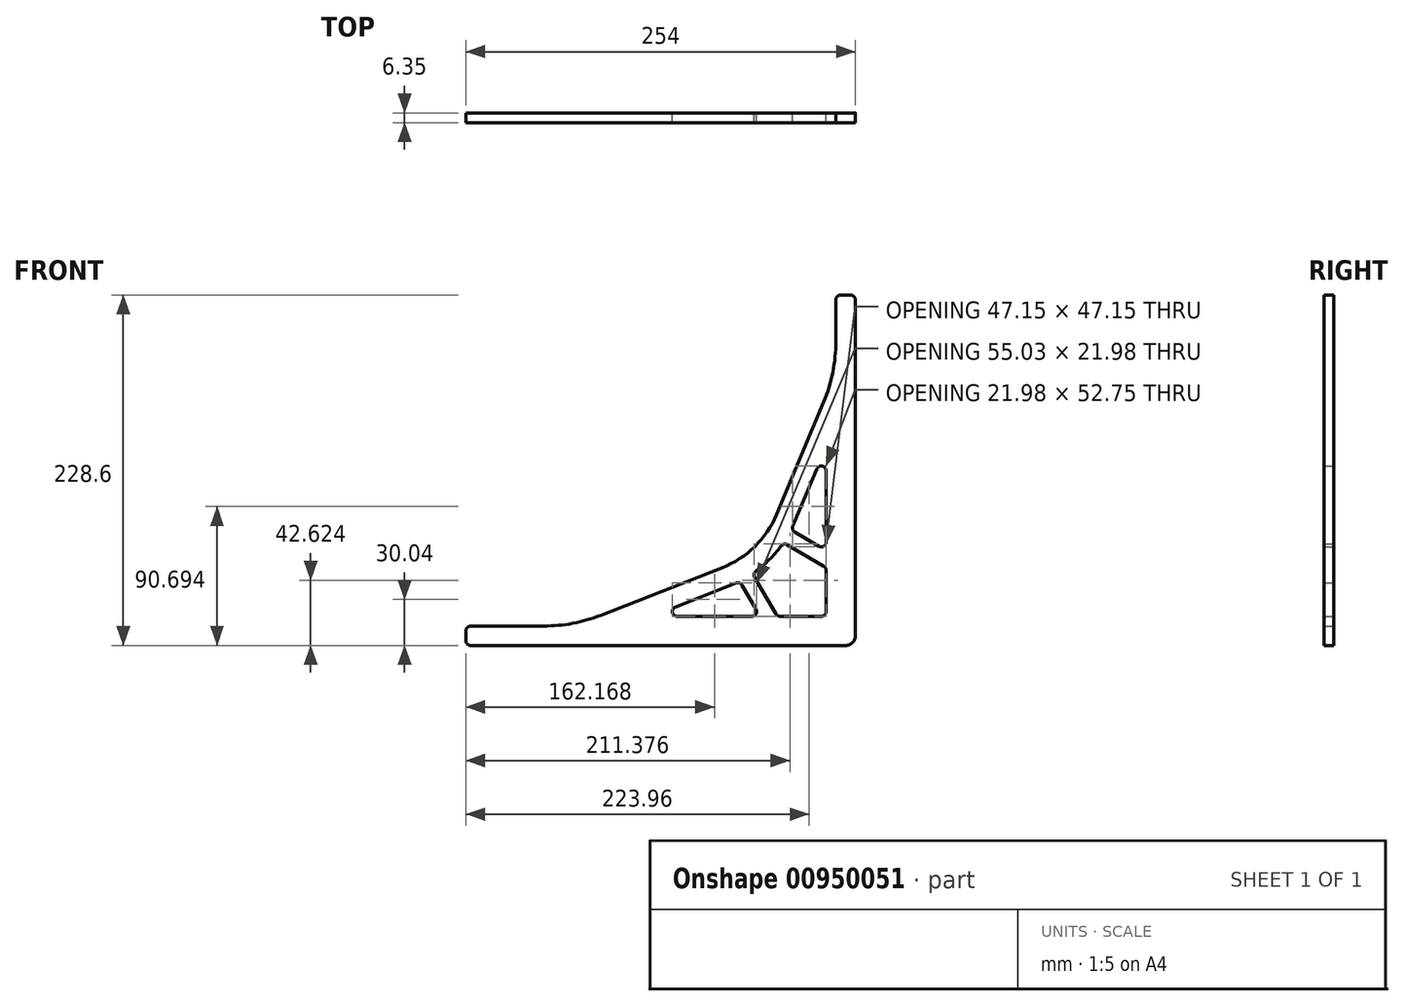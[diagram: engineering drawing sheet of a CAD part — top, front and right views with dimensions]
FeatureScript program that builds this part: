
annotation { "Feature Type Name" : "Feature", "Feature Type Description" : "" }
export const myFeature = defineFeature(function(context is Context, id is Id, definition is map)
    precondition{}
    {
        {
            var Q0;
            Q0=qCreatedBy(makeId("Front.planeOp"),FACE);
            var sketch = newSketch(context, id + "F0", { "sketchPlane" : qUnion([Q0])});
            skLineSegment(sketch, "E0", {"start": v(-254, 0) * mm, "end": v(-6.35, 0) * mm});
            skLineSegment(sketch, "E1", {"start": v(0, 6.35) * mm, "end": v(0, 228.6) * mm});
            skLineSegment(sketch, "E2", {"start": v(0, 228.6) * mm, "end": v(-12.7, 228.6) * mm});
            skLineSegment(sketch, "E3", {"start": v(-12.7, 228.6) * mm, "end": v(-12.7, 198.2) * mm});
            skLineSegment(sketch, "E4", {"start": v(-203.2, 12.7) * mm, "end": v(-254, 12.7) * mm});
            skLineSegment(sketch, "E5", {"start": v(-254, 12.7) * mm, "end": v(-254, 0) * mm});
            skLineSegment(sketch, "E6", {"start": v(-166.11, 19.71) * mm, "end": v(-86.76, 50.82) * mm});
            skLineSegment(sketch, "E7", {"start": v(-51.37, 85.42) * mm, "end": v(-20.58, 158.98) * mm});
            skPoint(sketch, "E8.visualSharp", {"position": v(-61.74, 60.63) * mm});
            skArc(sketch, "E8.filletArc", {"start": v(-86.76, 50.82) * mm, "mid": v(-65.55, 64.53) * mm, "end": v(-51.37, 85.42) * mm});
            skPoint(sketch, "E9.visualSharp", {"position": v(-12.7, 177.8) * mm});
            skArc(sketch, "E9.filletArc", {"start": v(-20.58, 158.98) * mm, "mid": v(-14.69, 178.2) * mm, "end": v(-12.7, 198.2) * mm});
            skPoint(sketch, "E10.visualSharp", {"position": v(-184, 12.7) * mm});
            skArc(sketch, "E10.filletArc", {"start": v(-203.2, 12.7) * mm, "mid": v(-184.33, 14.47) * mm, "end": v(-166.11, 19.71) * mm});
            skCircle(sketch, "E11", {"center": v(-38.1, 38.1) * mm, "radius": 38.1 * mm, "construction": true});
            skLineSegment(sketch, "E12", {"start": v(-109.94, 109.94) * mm, "end": v(-38.1, 38.1) * mm, "construction": true});
            skLineSegment(sketch, "E13", {"start": v(-82.13, 39) * mm, "end": v(-117.37, 25.18) * mm});
            skLineSegment(sketch, "E14", {"start": v(-116.21, 19.05) * mm, "end": v(-67.5, 19.05) * mm});
            skLineSegment(sketch, "E15", {"start": v(-64.76, 23.84) * mm, "end": v(-73.97, 39.47) * mm});
            skLineSegment(sketch, "E16", {"start": v(-25.15, 115.16) * mm, "end": v(-39.65, 80.52) * mm});
            skLineSegment(sketch, "E17", {"start": v(-39.47, 73.97) * mm, "end": v(-23.84, 64.76) * mm});
            skLineSegment(sketch, "E18", {"start": v(-19.05, 67.5) * mm, "end": v(-19.05, 113.93) * mm});
            skPoint(sketch, "E19.visualSharp", {"position": v(0, 0) * mm});
            skArc(sketch, "E19.filletArc", {"start": v(-6.35, 0) * mm, "mid": v(-1.86, 1.86) * mm, "end": v(0, 6.35) * mm});
            skCircle(sketch, "E20", {"center": v(-9.52, 9.52) * mm, "radius": 9.53 * mm, "construction": true});
            skCircle(sketch, "E21", {"center": v(-9.52, 50.8) * mm, "radius": 9.53 * mm, "construction": true});
            skCircle(sketch, "E22", {"center": v(-6.35, 222.25) * mm, "radius": 6.35 * mm, "construction": true});
            skCircle(sketch, "E23", {"center": v(-50.8, 9.52) * mm, "radius": 9.53 * mm, "construction": true});
            skCircle(sketch, "E24", {"center": v(-247.65, 6.35) * mm, "radius": 6.35 * mm, "construction": true});
            skArc(sketch, "E25", {"start": v(-82.13, 39) * mm, "mid": v(-80.07, 39.84) * mm, "end": v(-78.03, 40.75) * mm});
            skLineSegment(sketch, "E26", {"start": v(-65.76, 44.3) * mm, "end": v(-51.8, 20.61) * mm});
            skLineSegment(sketch, "E27", {"start": v(-49.07, 19.05) * mm, "end": v(-22.22, 19.05) * mm});
            skLineSegment(sketch, "E28", {"start": v(-19.05, 22.22) * mm, "end": v(-19.05, 49.07) * mm});
            skLineSegment(sketch, "E29", {"start": v(-20.61, 51.8) * mm, "end": v(-44.3, 65.76) * mm});
            skCircle(sketch, "E30", {"center": v(-60.55, 60.55) * mm, "radius": 6.35 * mm, "construction": true});
            skLineSegment(sketch, "E31", {"start": v(-109.94, 109.94) * mm, "end": v(-50.8, 9.52) * mm, "construction": true});
            skLineSegment(sketch, "E32", {"start": v(-9.52, 50.8) * mm, "end": v(-109.94, 109.94) * mm, "construction": true});
            skCircle(sketch, "E33", {"center": v(-39.53, 68.47) * mm, "radius": 4.76 * mm, "construction": true});
            skCircle(sketch, "E34", {"center": v(-68.33, 39.3) * mm, "radius": 4.76 * mm, "construction": true});
            skPoint(sketch, "E35.visualSharp", {"position": v(-50.88, 19.05) * mm});
            skArc(sketch, "E35.filletArc", {"start": v(-51.8, 20.61) * mm, "mid": v(-50.64, 19.47) * mm, "end": v(-49.07, 19.05) * mm});
            skArc(sketch, "E36.filletArc", {"start": v(-64.9, 48.48) * mm, "mid": v(-66.13, 46.56) * mm, "end": v(-65.76, 44.3) * mm});
            skPoint(sketch, "E37.visualSharp", {"position": v(-19.05, 50.88) * mm});
            skArc(sketch, "E37.filletArc", {"start": v(-19.05, 49.07) * mm, "mid": v(-19.47, 50.64) * mm, "end": v(-20.61, 51.8) * mm});
            skPoint(sketch, "E38.visualSharp", {"position": v(-46.83, 67.24) * mm});
            skArc(sketch, "E38.filletArc", {"start": v(-44.3, 65.76) * mm, "mid": v(-46.56, 66.13) * mm, "end": v(-48.48, 64.9) * mm});
            skPoint(sketch, "E39.visualSharp", {"position": v(-19.05, 19.05) * mm});
            skArc(sketch, "E39.filletArc", {"start": v(-22.22, 19.05) * mm, "mid": v(-19.98, 19.98) * mm, "end": v(-19.05, 22.22) * mm});
            skPoint(sketch, "E40.visualSharp", {"position": v(-133, 19.05) * mm});
            skArc(sketch, "E40.filletArc", {"start": v(-117.37, 25.18) * mm, "mid": v(-119.33, 21.64) * mm, "end": v(-116.21, 19.05) * mm});
            skPoint(sketch, "E41.visualSharp", {"position": v(-61.94, 19.05) * mm});
            skArc(sketch, "E41.filletArc", {"start": v(-67.5, 19.05) * mm, "mid": v(-64.74, 20.65) * mm, "end": v(-64.76, 23.84) * mm});
            skPoint(sketch, "E42.visualSharp", {"position": v(-19.05, 129.74) * mm});
            skArc(sketch, "E42.filletArc", {"start": v(-19.05, 113.93) * mm, "mid": v(-21.6, 117.04) * mm, "end": v(-25.15, 115.16) * mm});
            skPoint(sketch, "E43.visualSharp", {"position": v(-19.05, 61.94) * mm});
            skArc(sketch, "E43.filletArc", {"start": v(-23.84, 64.76) * mm, "mid": v(-20.65, 64.74) * mm, "end": v(-19.05, 67.5) * mm});
            skArc(sketch, "E44.trimOffspring", {"start": v(-40.75, 78.03) * mm, "mid": v(-40.19, 79.27) * mm, "end": v(-39.65, 80.52) * mm});
            skArc(sketch, "E45.trimOffspring", {"start": v(-64.9, 48.48) * mm, "mid": v(-56.06, 56.06) * mm, "end": v(-48.48, 64.9) * mm});
            skPoint(sketch, "E46.visualSharp", {"position": v(-75.45, 42) * mm});
            skArc(sketch, "E46.filletArc", {"start": v(-73.97, 39.47) * mm, "mid": v(-75.75, 40.9) * mm, "end": v(-78.03, 40.75) * mm});
            skPoint(sketch, "E47.visualSharp", {"position": v(-42, 75.45) * mm});
            skArc(sketch, "E47.filletArc", {"start": v(-40.75, 78.03) * mm, "mid": v(-40.9, 75.75) * mm, "end": v(-39.47, 73.97) * mm});
            skSolve(sketch);
        }
        {
            var Q0;
            Q0=makeQuery(id+"F0.imprint","IMPRINT",FACE,{"disambiguationData":[TD([[makeQuery(id+"F0.imprint","IMPRINT",EDGE,{"derivedFrom":sQuery(id+"F0.wireOp",EDGE,"E0")}),1.0]])]});
            extrude(context, id + "F1", {"entities" : qUnion([Q0]), "depth" : 6.35 * mm, "offsetDistance" : 25.4 * mm});
        }
        {
            var Q0;
            Q0=makeQuery(id+"F1.opExtrude","SWEPT_EDGE",EDGE,{"disambiguationData":[OSD([sQuery(id+"F0.wireOp",EDGE,"E0"),sQuery(id+"F0.wireOp",EDGE,"E5")])]});
            var Q1;
            Q1=makeQuery(id+"F1.opExtrude","SWEPT_EDGE",EDGE,{"disambiguationData":[OSD([sQuery(id+"F0.wireOp",EDGE,"E4"),sQuery(id+"F0.wireOp",EDGE,"E5")])]});
            var Q2;
            Q2=makeQuery(id+"F1.opExtrude","SWEPT_EDGE",EDGE,{"disambiguationData":[OSD([sQuery(id+"F0.wireOp",EDGE,"E1"),sQuery(id+"F0.wireOp",EDGE,"E2")])]});
            var Q3;
            Q3=makeQuery(id+"F1.opExtrude","SWEPT_EDGE",EDGE,{"disambiguationData":[OSD([sQuery(id+"F0.wireOp",EDGE,"E2"),sQuery(id+"F0.wireOp",EDGE,"E3")])]});
            fillet(context, id + "F2", {"entities" : qUnion([Q0, Q1, Q2, Q3]), "radius" : 3.17 * mm, "tangentPropagation" : true, "allowEdgeOverflow" : false});
        }
    });
